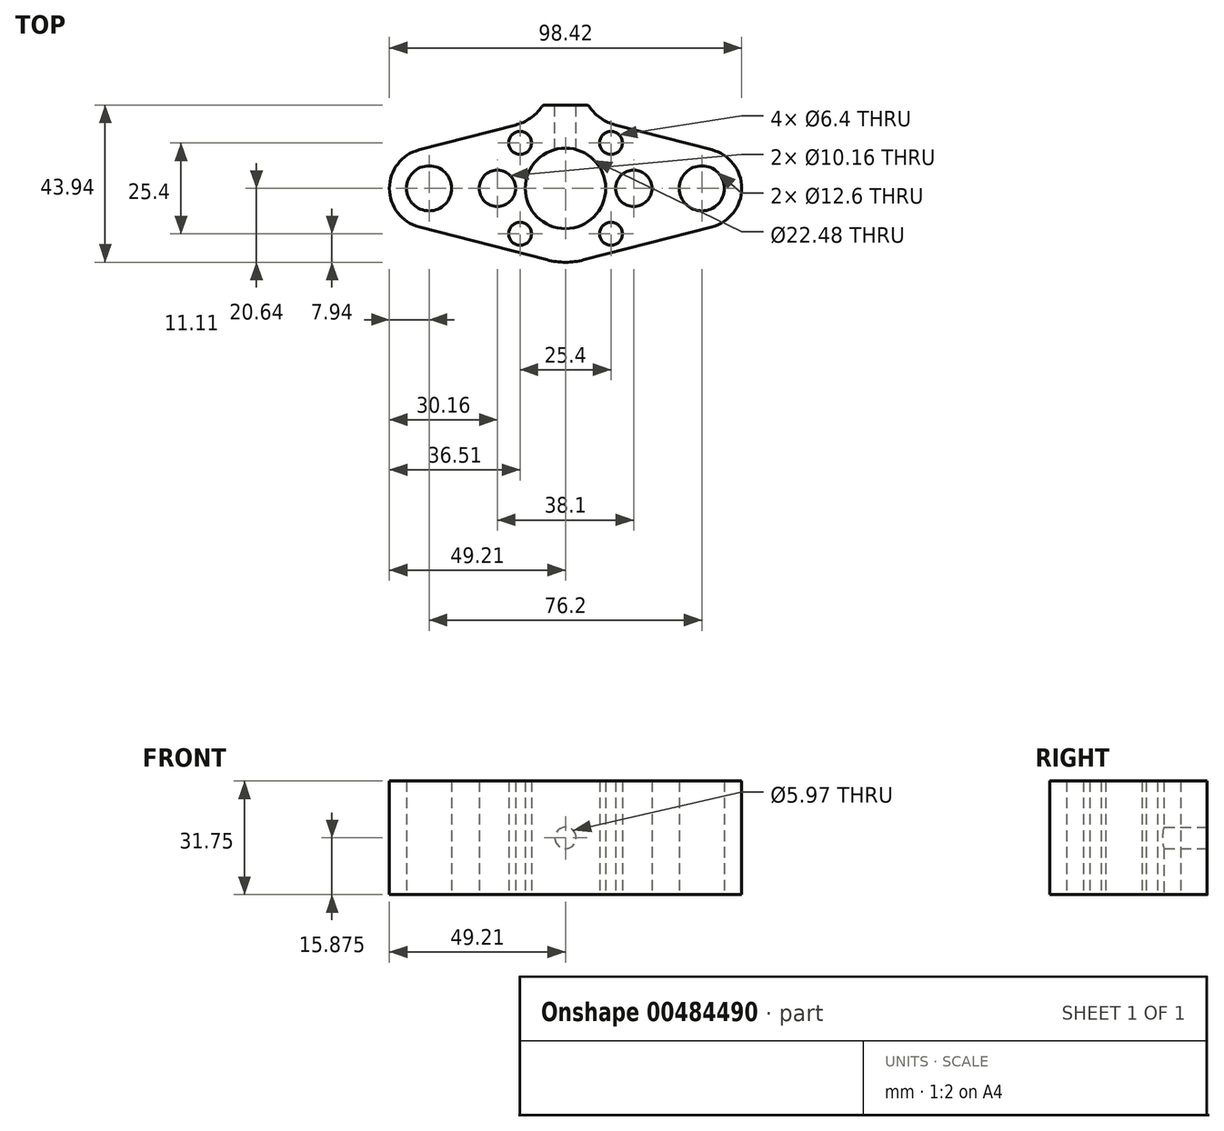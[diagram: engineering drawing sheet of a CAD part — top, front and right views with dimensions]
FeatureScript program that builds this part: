
annotation { "Feature Type Name" : "Feature", "Feature Type Description" : "" }
export const myFeature = defineFeature(function(context is Context, id is Id, definition is map)
    precondition{}
    {
        {
            var Q0;
            Q0=qCreatedBy(makeId("Top.planeOp"),FACE);
            var sketch = newSketch(context, id + "F0", { "sketchPlane" : qUnion([Q0])});
            skCircle(sketch, "E0", {"center": v(0, 0) * mm, "radius": 11.24 * mm});
            skCircle(sketch, "E1", {"center": v(-19.05, 0) * mm, "radius": 5.08 * mm});
            skCircle(sketch, "E2", {"center": v(19.05, 0) * mm, "radius": 5.08 * mm});
            skLineSegment(sketch, "E3", {"start": v(-19.05, 0) * mm, "end": v(19.05, 0) * mm, "construction": true});
            skCircle(sketch, "E4", {"center": v(-38.1, 0) * mm, "radius": 6.3 * mm});
            skCircle(sketch, "E5", {"center": v(38.1, 0) * mm, "radius": 6.3 * mm});
            skLineSegment(sketch, "E6", {"start": v(-19.05, 0) * mm, "end": v(-38.1, 0) * mm, "construction": true});
            skLineSegment(sketch, "E7", {"start": v(19.05, 0) * mm, "end": v(38.1, 0) * mm, "construction": true});
            skArc(sketch, "E8", {"start": v(-40.88, 10.76) * mm, "mid": v(-49.21, 0) * mm, "end": v(-40.88, -10.76) * mm});
            skArc(sketch, "E9", {"start": v(40.88, -10.76) * mm, "mid": v(49.21, 0) * mm, "end": v(40.88, 10.76) * mm});
            skArc(sketch, "E10", {"start": v(-5.16, -19.98) * mm, "mid": v(0, -20.64) * mm, "end": v(5.16, -19.98) * mm});
            skLineSegment(sketch, "E11", {"start": v(-40.88, 10.76) * mm, "end": v(-5.16, 19.98) * mm});
            skLineSegment(sketch, "E12", {"start": v(5.16, 19.98) * mm, "end": v(40.88, 10.76) * mm});
            skLineSegment(sketch, "E13", {"start": v(-40.88, -10.76) * mm, "end": v(-5.16, -19.98) * mm});
            skLineSegment(sketch, "E14", {"start": v(5.16, -19.98) * mm, "end": v(40.88, -10.76) * mm});
            skArc(sketch, "E15.trimOffspring", {"start": v(5.16, 19.98) * mm, "mid": v(0, 20.64) * mm, "end": v(-5.16, 19.98) * mm});
            skLineSegment(sketch, "E16.bottom", {"start": v(-12.7, 12.7) * mm, "end": v(12.7, 12.7) * mm, "construction": true});
            skLineSegment(sketch, "E16.top", {"start": v(-12.7, -12.7) * mm, "end": v(12.7, -12.7) * mm, "construction": true});
            skLineSegment(sketch, "E16.left", {"start": v(-12.7, 12.7) * mm, "end": v(-12.7, -12.7) * mm, "construction": true});
            skLineSegment(sketch, "E16.right", {"start": v(12.7, 12.7) * mm, "end": v(12.7, -12.7) * mm, "construction": true});
            skCircle(sketch, "E17", {"center": v(-12.7, 12.7) * mm, "radius": 3.2 * mm});
            skCircle(sketch, "E18", {"center": v(-12.7, -12.7) * mm, "radius": 3.2 * mm});
            skCircle(sketch, "E19", {"center": v(12.7, -12.7) * mm, "radius": 3.2 * mm});
            skCircle(sketch, "E20", {"center": v(12.7, 12.7) * mm, "radius": 3.2 * mm});
            skSolve(sketch);
        }
        {
            var Q0;
            Q0 = qSketchRegion(id + "F0", true);
            extrude(context, id + "F1", {"entities" : qUnion([Q0]), "depth" : 31.75 * mm});
        }
        {
            var Q0;
            Q0=makeQuery(id+"F1.opExtrude","CAP_FACE",FACE,{"disambiguationData":[OSD([sQuery(id+"F0.wireOp",EDGE,"E0"),sQuery(id+"F0.wireOp",EDGE,"E1"),sQuery(id+"F0.wireOp",EDGE,"E2"),sQuery(id+"F0.wireOp",EDGE,"E4"),sQuery(id+"F0.wireOp",EDGE,"E5"),sQuery(id+"F0.wireOp",EDGE,"E8"),sQuery(id+"F0.wireOp",EDGE,"E9"),sQuery(id+"F0.wireOp",EDGE,"E10"),sQuery(id+"F0.wireOp",EDGE,"E11"),sQuery(id+"F0.wireOp",EDGE,"E12"),sQuery(id+"F0.wireOp",EDGE,"E13"),sQuery(id+"F0.wireOp",EDGE,"E14"),sQuery(id+"F0.wireOp",EDGE,"E15.trimOffspring"),sQuery(id+"F0.wireOp",EDGE,"E17"),sQuery(id+"F0.wireOp",EDGE,"E18"),sQuery(id+"F0.wireOp",EDGE,"E19"),sQuery(id+"F0.wireOp",EDGE,"E20")])],"isStart":false});
            var sketch = newSketch(context, id + "F2", { "sketchPlane" : qUnion([Q0])});
            skLineSegment(sketch, "E21", {"start": v(-6.35, 23.3) * mm, "end": v(6.35, 23.3) * mm});
            skLineSegment(sketch, "E22", {"start": v(0, 23.3) * mm, "end": v(0, 0) * mm, "construction": true});
            skLineSegment(sketch, "E23", {"start": v(-6.35, 23.3) * mm, "end": v(-6.35, 18.2) * mm});
            skLineSegment(sketch, "E24", {"start": v(-6.35, 18.2) * mm, "end": v(6.35, 18.2) * mm});
            skLineSegment(sketch, "E25", {"start": v(6.35, 18.2) * mm, "end": v(6.35, 23.3) * mm});
            skSolve(sketch);
        }
        {
            var Q0;
            Q0 = qSketchRegion(id + "F2", true);
            extrude(context, id + "F3", {"entities" : qUnion([Q0]), "operationType" : NewBodyOperationType.ADD, "oppositeDirection" : true, "depth" : 31.75 * mm});
        }
        {
            var Q0;
            Q0=makeQuery(id+"F3.boolean.opBoolean","INTERSECT",EDGE,{"derivedFrom":[makeQuery(id+"F1.opExtrude","SWEPT_FACE",FACE,{"disambiguationData":[OSD([sQuery(id+"F0.wireOp",EDGE,"E11")])]}),makeQuery(id+"F3.opExtrude","SWEPT_FACE",FACE,{"disambiguationData":[OSD([sQuery(id+"F2.wireOp",EDGE,"E23")])]})]});
            var Q1;
            Q1=makeQuery(id+"F3.boolean.opBoolean","INTERSECT",EDGE,{"derivedFrom":[makeQuery(id+"F1.opExtrude","SWEPT_FACE",FACE,{"disambiguationData":[OSD([sQuery(id+"F0.wireOp",EDGE,"E12")])]}),makeQuery(id+"F3.opExtrude","SWEPT_FACE",FACE,{"disambiguationData":[OSD([sQuery(id+"F2.wireOp",EDGE,"E25")])]})]});
            fillet(context, id + "F4", {"entities" : qUnion([Q0, Q1]), "radius" : 12.7 * mm, "tangentPropagation" : true, "allowEdgeOverflow" : false});
        }
        {
            var Q0;
            Q0=makeQuery(id+"F4.opFillet","BLEND_EDGE",EDGE,{"blendedFrom":[makeQuery(id+"F3.boolean.opBoolean","INTERSECT",EDGE,{"derivedFrom":[makeQuery(id+"F1.opExtrude","SWEPT_FACE",FACE,{"disambiguationData":[OSD([sQuery(id+"F0.wireOp",EDGE,"E11")])]}),makeQuery(id+"F3.opExtrude","SWEPT_FACE",FACE,{"disambiguationData":[OSD([sQuery(id+"F2.wireOp",EDGE,"E23")])]})]}),makeQuery(id+"F3.opExtrude","SWEPT_FACE",FACE,{"disambiguationData":[OSD([sQuery(id+"F2.wireOp",EDGE,"E21")])]})],"blendedInto":[makeQuery(id+"F3.opExtrude","SWEPT_FACE",FACE,{"disambiguationData":[OSD([sQuery(id+"F2.wireOp",EDGE,"E21")])]})]});
            var Q1;
            Q1=makeQuery(id+"F4.opFillet","BLEND_EDGE",EDGE,{"blendedFrom":[makeQuery(id+"F3.boolean.opBoolean","INTERSECT",EDGE,{"derivedFrom":[makeQuery(id+"F1.opExtrude","SWEPT_FACE",FACE,{"disambiguationData":[OSD([sQuery(id+"F0.wireOp",EDGE,"E12")])]}),makeQuery(id+"F3.opExtrude","SWEPT_FACE",FACE,{"disambiguationData":[OSD([sQuery(id+"F2.wireOp",EDGE,"E25")])]})]}),makeQuery(id+"F3.opExtrude","SWEPT_FACE",FACE,{"disambiguationData":[OSD([sQuery(id+"F2.wireOp",EDGE,"E21")])]})],"blendedInto":[makeQuery(id+"F3.opExtrude","SWEPT_FACE",FACE,{"disambiguationData":[OSD([sQuery(id+"F2.wireOp",EDGE,"E21")])]})]});
            fillet(context, id + "F5", {"entities" : qUnion([Q0, Q1]), "radius" : 1.27 * mm, "tangentPropagation" : true, "allowEdgeOverflow" : false});
        }
        {
            var Q0;
            Q0=makeQuery(id+"F3.opExtrude","SWEPT_FACE",FACE,{"disambiguationData":[OSD([sQuery(id+"F2.wireOp",EDGE,"E21")])]});
            var sketch = newSketch(context, id + "F6", { "sketchPlane" : qUnion([Q0])});
            skCircle(sketch, "E26", {"center": v(0, 15.88) * mm, "radius": 2.98 * mm});
            skLineSegment(sketch, "E27", {"start": v(-5.67, 15.88) * mm, "end": v(0, 15.88) * mm, "construction": true});
            skSolve(sketch);
        }
        {
            var Q0;
            Q0 = qSketchRegion(id + "F6", true);
            extrude(context, id + "F7", {"entities" : qUnion([Q0]), "operationType" : NewBodyOperationType.REMOVE, "oppositeDirection" : true, "depth" : 25.4 * mm});
        }
    });
